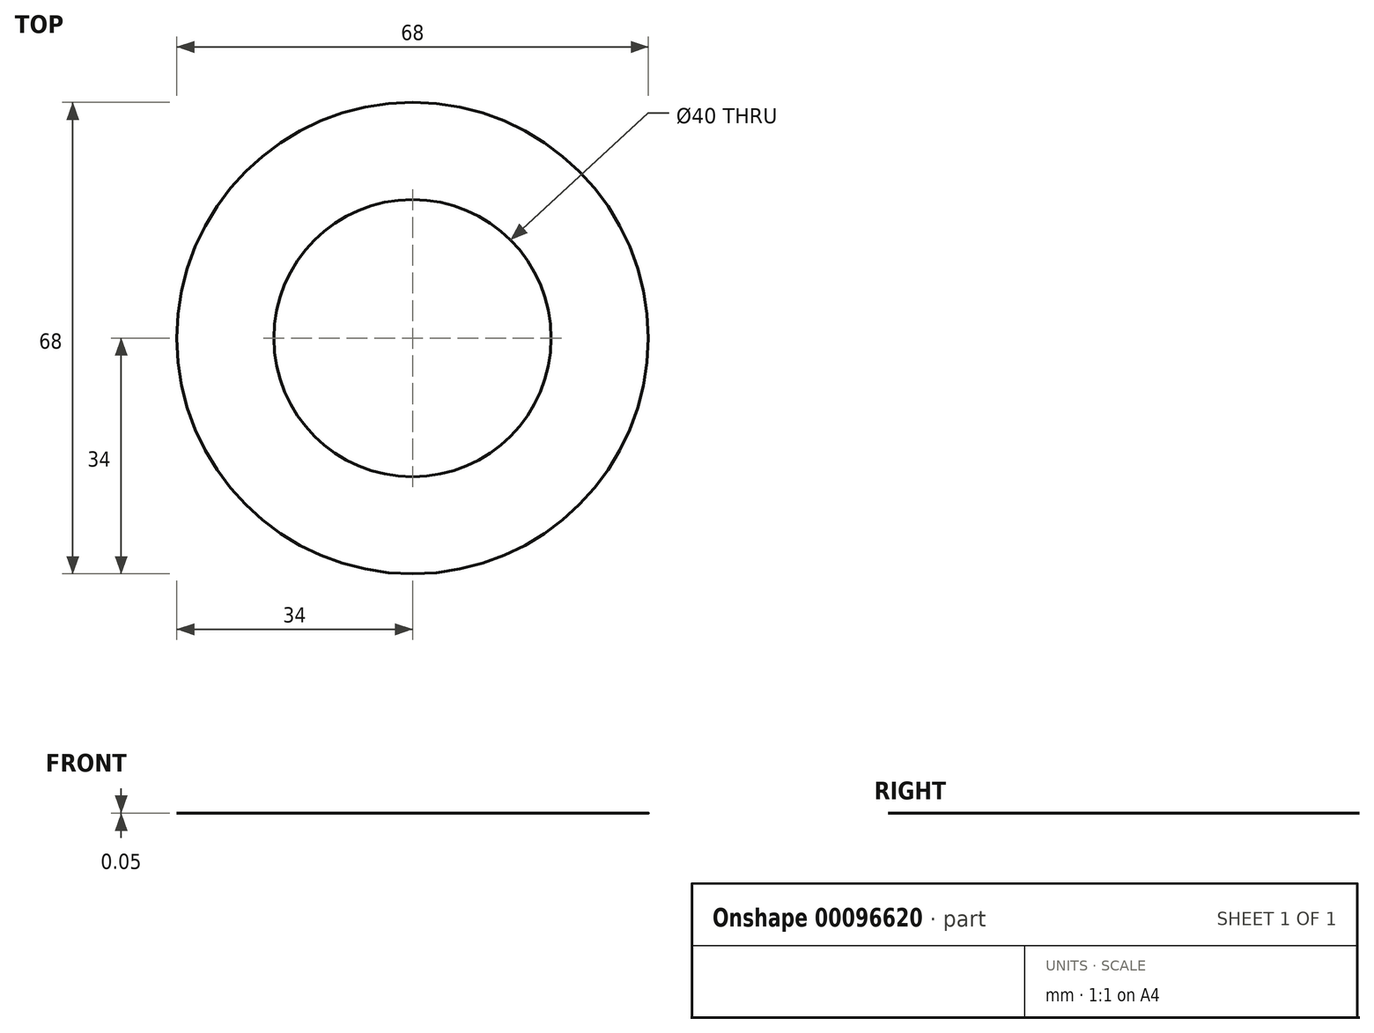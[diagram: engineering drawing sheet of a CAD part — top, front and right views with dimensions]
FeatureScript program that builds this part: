
annotation { "Feature Type Name" : "Feature", "Feature Type Description" : "" }
export const myFeature = defineFeature(function(context is Context, id is Id, definition is map)
    precondition{}
    {
        {
            var Q0;
            Q0=qCreatedBy(makeId("Top.planeOp"),FACE);
            var sketch = newSketch(context, id + "F0", { "sketchPlane" : qUnion([Q0])});
            skCircle(sketch, "E0", {"center": v(0, 0) * mm, "radius": 20 * mm});
            skCircle(sketch, "E1", {"center": v(0, 0) * mm, "radius": 26.5 * mm});
            skCircle(sketch, "E2", {"center": v(0, 0) * mm, "radius": 34 * mm});
            skSolve(sketch);
        }
        {
            var Q0;
            Q0=makeQuery(id+"F0.imprint","IMPRINT",FACE,{"disambiguationData":[TD([[makeQuery(id+"F0.imprint","IMPRINT",EDGE,{"derivedFrom":sQuery(id+"F0.wireOp",EDGE,"E1")}),-1.0]])]});
            var Q1;
            Q1=makeQuery(id+"F0.imprint","IMPRINT",FACE,{"disambiguationData":[TD([[makeQuery(id+"F0.imprint","IMPRINT",EDGE,{"derivedFrom":sQuery(id+"F0.wireOp",EDGE,"E0")}),-1.0]])]});
            extrude(context, id + "F1", {"entities" : qUnion([Q0, Q1]), "depth" : 0.05 * mm});
        }
    });
